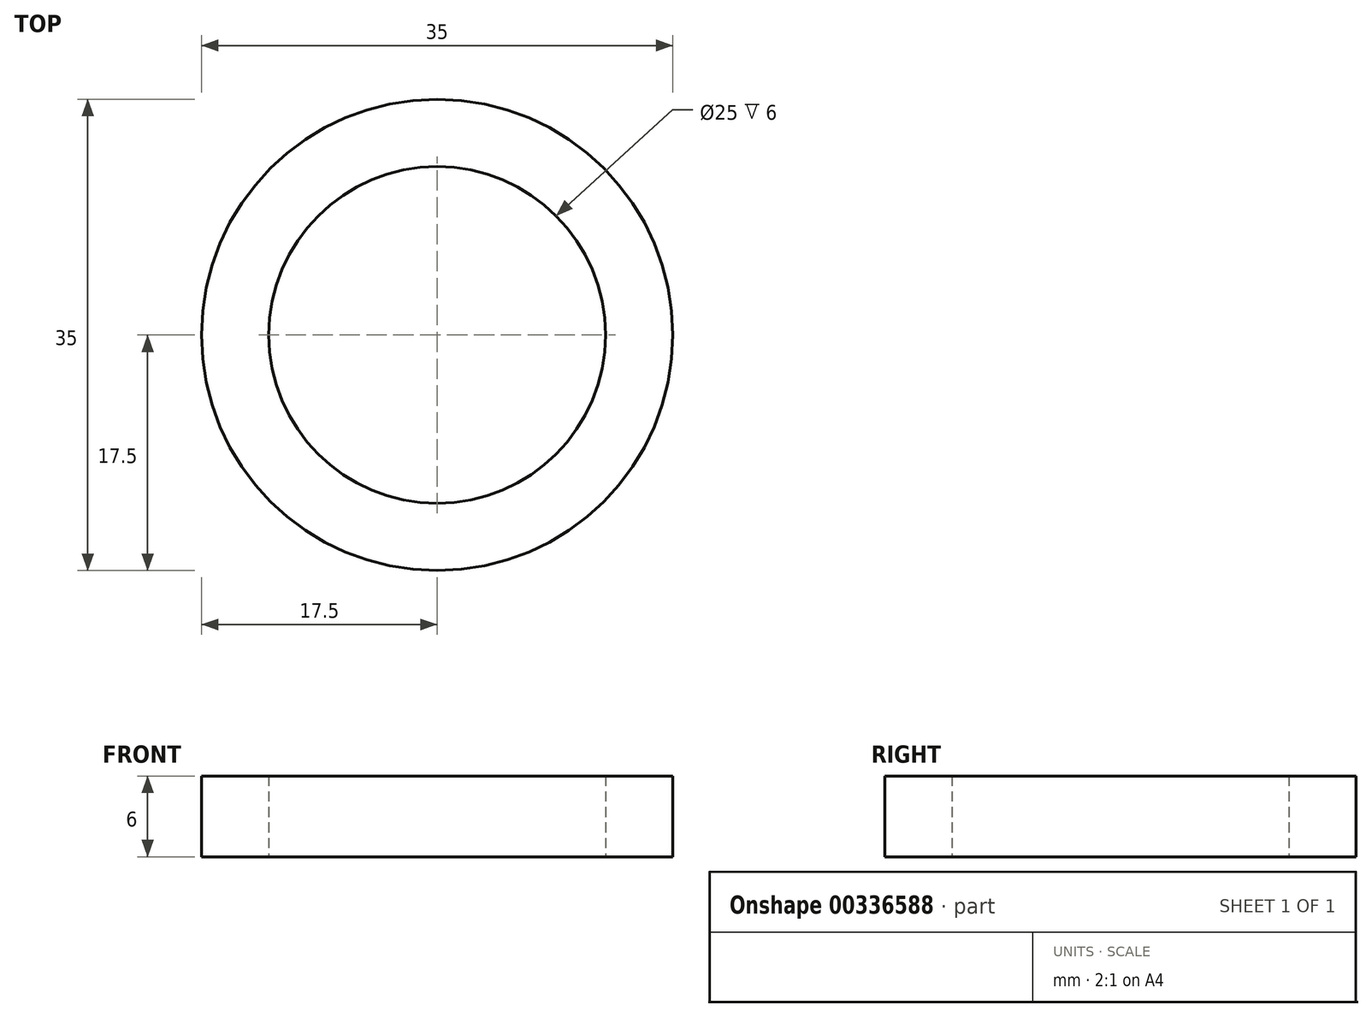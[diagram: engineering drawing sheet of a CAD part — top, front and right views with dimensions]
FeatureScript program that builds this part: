
annotation { "Feature Type Name" : "Feature", "Feature Type Description" : "" }
export const myFeature = defineFeature(function(context is Context, id is Id, definition is map)
    precondition{}
    {
        {
            var Q0;
            Q0=qCreatedBy(makeId("Top.planeOp"),FACE);
            var sketch = newSketch(context, id + "F0", { "sketchPlane" : qUnion([Q0])});
            skCircle(sketch, "E0", {"center": v(0, 0) * mm, "radius": 12.5 * mm});
            skCircle(sketch, "E1.0", {"center": v(0, 0) * mm, "radius": 17.5 * mm});
            skSolve(sketch);
        }
        {
            var Q0;
            Q0=makeQuery(id+"F0.imprint","IMPRINT",FACE,{"disambiguationData":[TD([[makeQuery(id+"F0.imprint","IMPRINT",EDGE,{"derivedFrom":sQuery(id+"F0.wireOp",EDGE,"E0")}),-1.0]])]});
            extrude(context, id + "F1", {"entities" : qUnion([Q0]), "depth" : 6 * mm});
        }
    });
